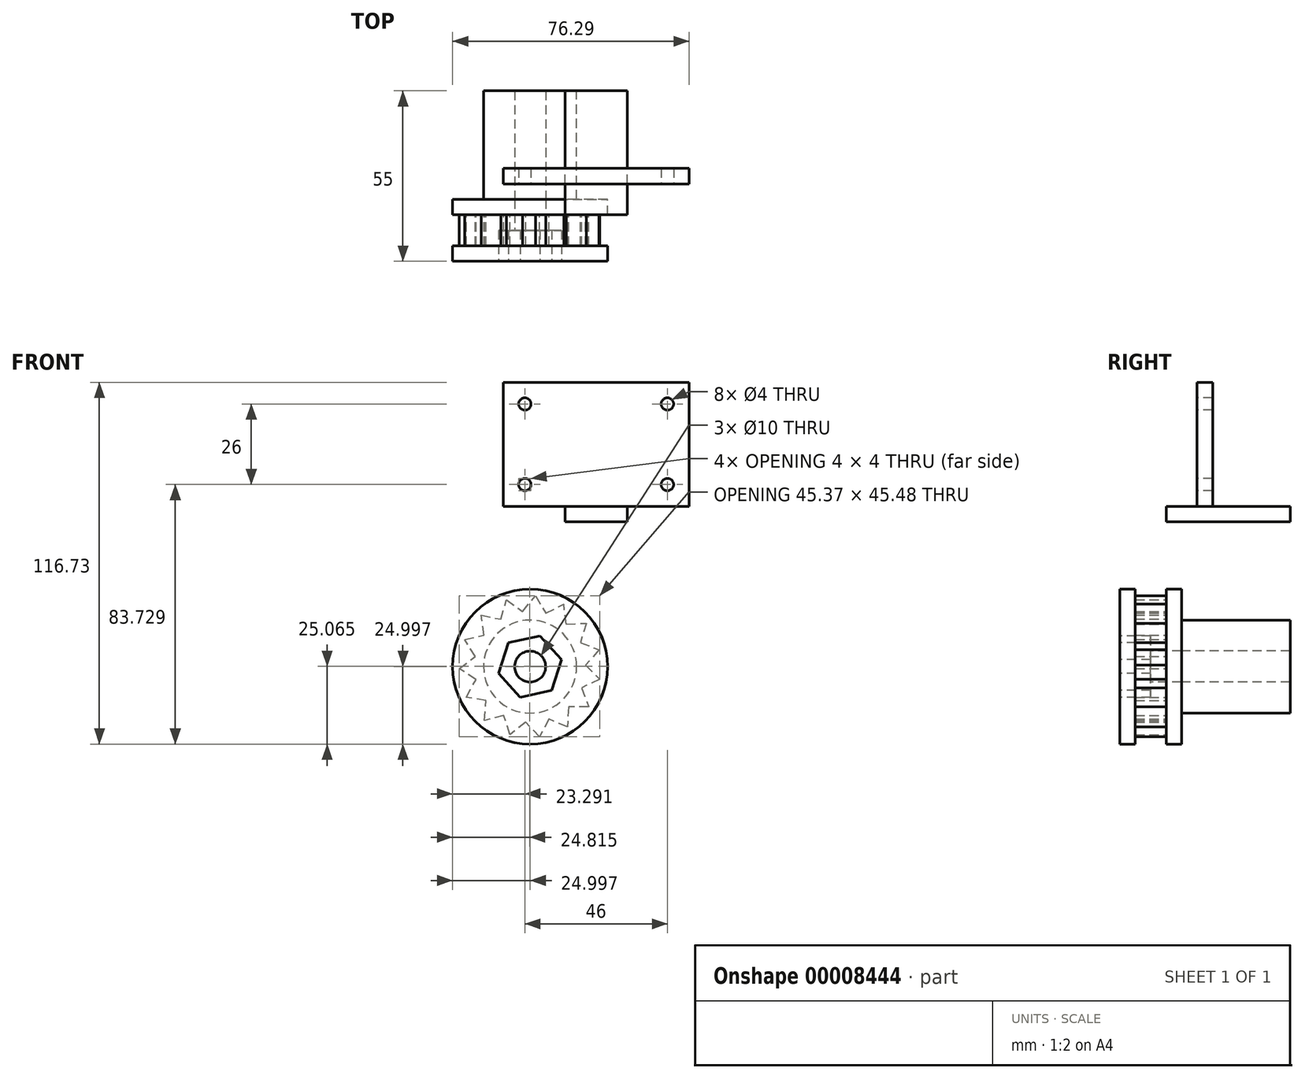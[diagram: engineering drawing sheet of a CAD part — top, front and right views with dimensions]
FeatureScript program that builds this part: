
annotation { "Feature Type Name" : "Feature", "Feature Type Description" : "" }
export const myFeature = defineFeature(function(context is Context, id is Id, definition is map)
    precondition{}
    {
        {
            var Q0;
            Q0=qCreatedBy(makeId("Front.planeOp"),FACE);
            var sketch = newSketch(context, id + "F0", { "sketchPlane" : qUnion([Q0])});
            skLineSegment(sketch, "E0", {"start": v(-23.94, 12.62) * mm, "end": v(-23.94, 7.62) * mm});
            skLineSegment(sketch, "E1", {"start": v(-23.94, 7.62) * mm, "end": v(-3.94, 7.62) * mm});
            skLineSegment(sketch, "E2", {"start": v(-3.94, 7.62) * mm, "end": v(-3.94, 12.62) * mm});
            skLineSegment(sketch, "E3", {"start": v(-3.94, 12.62) * mm, "end": v(16.06, 12.62) * mm});
            skLineSegment(sketch, "E4", {"start": v(16.06, 12.62) * mm, "end": v(16.06, 52.62) * mm});
            skLineSegment(sketch, "E5", {"start": v(16.06, 52.62) * mm, "end": v(-43.94, 52.62) * mm});
            skLineSegment(sketch, "E6", {"start": v(-43.94, 52.62) * mm, "end": v(-43.94, 12.62) * mm});
            skLineSegment(sketch, "E7", {"start": v(-43.94, 12.62) * mm, "end": v(-23.94, 12.62) * mm});
            skSolve(sketch);
        }
        {
            var Q0;
            Q0=makeQuery(id+"F0.imprint","IMPRINT",FACE,{"disambiguationData":[TD([[makeQuery(id+"F0.imprint","IMPRINT",EDGE,{"derivedFrom":sQuery(id+"F0.wireOp",EDGE,"E0")}),1.0]])]});
            extrude(context, id + "F1", {"entities" : qUnion([Q0]), "depth" : 40 * mm});
        }
        {
            var Q0;
            Q0=makeQuery(id+"F1.opExtrude","SWEPT_FACE",FACE,{"disambiguationData":[OSD([sQuery(id+"F0.wireOp",EDGE,"E6")])]});
            var sketch = newSketch(context, id + "F2", { "sketchPlane" : qUnion([Q0])});
            skLineSegment(sketch, "E8", {"start": v(40, 12.62) * mm, "end": v(30, 12.62) * mm});
            skLineSegment(sketch, "E9", {"start": v(30, 12.62) * mm, "end": v(30, 52.62) * mm});
            skLineSegment(sketch, "E10", {"start": v(30, 52.62) * mm, "end": v(40, 52.62) * mm});
            skLineSegment(sketch, "E11", {"start": v(40, 52.62) * mm, "end": v(40, 12.62) * mm});
            skSolve(sketch);
        }
        {
            var Q0;
            Q0=makeQuery(id+"F2.imprint","IMPRINT",FACE,{"disambiguationData":[TD([[makeQuery(id+"F2.imprint","IMPRINT",EDGE,{"derivedFrom":sQuery(id+"F2.wireOp",EDGE,"E8")}),-1.0]])]});
            var Q1;
            Q1=makeQuery(id+"F1.opExtrude","SWEPT_FACE",FACE,{"disambiguationData":[OSD([sQuery(id+"F0.wireOp",EDGE,"E4")])]});
            extrude(context, id + "F3", {"entities" : qUnion([Q0]), "operationType" : NewBodyOperationType.REMOVE, "endBound" : BoundingType.UP_TO_BODY, "oppositeDirection" : true, "endBoundEntityBody" : qUnion([Q1]), "depth" : 25 * mm});
        }
        {
            var Q0;
            Q0=makeQuery(id+"F1.opExtrude","SWEPT_FACE",FACE,{"disambiguationData":[OSD([sQuery(id+"F0.wireOp",EDGE,"E6")])]});
            var sketch = newSketch(context, id + "F4", { "sketchPlane" : qUnion([Q0])});
            skLineSegment(sketch, "E12.bottom", {"start": v(0, 52.62) * mm, "end": v(25, 52.62) * mm});
            skLineSegment(sketch, "E12.top", {"start": v(0, 12.62) * mm, "end": v(25, 12.62) * mm});
            skLineSegment(sketch, "E12.left", {"start": v(0, 52.62) * mm, "end": v(0, 12.62) * mm});
            skLineSegment(sketch, "E12.right", {"start": v(25, 52.62) * mm, "end": v(25, 12.62) * mm});
            skPoint(sketch, "E13", {"position": v(30, 52.62) * mm});
            skSolve(sketch);
        }
        {
            var Q0;
            Q0=makeQuery(id+"F4.imprint","IMPRINT",FACE,{"disambiguationData":[TD([[makeQuery(id+"F4.imprint","IMPRINT",EDGE,{"derivedFrom":sQuery(id+"F4.wireOp",EDGE,"E12.bottom")}),1.0]])]});
            extrude(context, id + "F5", {"entities" : qUnion([Q0]), "operationType" : NewBodyOperationType.REMOVE, "endBound" : BoundingType.THROUGH_ALL, "oppositeDirection" : true, "depth" : 25 * mm});
        }
        {
            var Q0;
            Q0=makeQuery(id+"F3.boolean.opBoolean","COPY",FACE,{"derivedFrom":makeQuery(id+"F3.opExtrude","SWEPT_FACE",FACE,{"disambiguationData":[OSD([sQuery(id+"F2.wireOp",EDGE,"E9")])]})});
            var sketch = newSketch(context, id + "F6", { "sketchPlane" : qUnion([Q0])});
            skCircle(sketch, "E14", {"center": v(-36.94, 45.62) * mm, "radius": 2 * mm});
            skCircle(sketch, "E15", {"center": v(-36.94, 19.62) * mm, "radius": 2 * mm});
            skCircle(sketch, "E16", {"center": v(9.06, 19.62) * mm, "radius": 2 * mm});
            skCircle(sketch, "E17", {"center": v(9.06, 45.62) * mm, "radius": 2 * mm});
            skSolve(sketch);
        }
        {
            var Q0;
            Q0=makeQuery(id+"F6.imprint","IMPRINT",FACE,{"disambiguationData":[TD([[makeQuery(id+"F6.imprint","IMPRINT",EDGE,{"derivedFrom":sQuery(id+"F6.wireOp",EDGE,"E14")}),1.0]])]});
            var Q1;
            Q1=makeQuery(id+"F6.imprint","IMPRINT",FACE,{"disambiguationData":[TD([[makeQuery(id+"F6.imprint","IMPRINT",EDGE,{"derivedFrom":sQuery(id+"F6.wireOp",EDGE,"E17")}),1.0]])]});
            var Q2;
            Q2=makeQuery(id+"F6.imprint","IMPRINT",FACE,{"disambiguationData":[TD([[makeQuery(id+"F6.imprint","IMPRINT",EDGE,{"derivedFrom":sQuery(id+"F6.wireOp",EDGE,"E16")}),1.0]])]});
            var Q3;
            Q3=makeQuery(id+"F6.imprint","IMPRINT",FACE,{"disambiguationData":[TD([[makeQuery(id+"F6.imprint","IMPRINT",EDGE,{"derivedFrom":sQuery(id+"F6.wireOp",EDGE,"E15")}),1.0]])]});
            extrude(context, id + "F7", {"entities" : qUnion([Q0, Q1, Q2, Q3]), "operationType" : NewBodyOperationType.REMOVE, "endBound" : BoundingType.THROUGH_ALL, "oppositeDirection" : true, "depth" : 25 * mm});
        }
        {
            var Q0;
            Q0=qCreatedBy(makeId("Front.planeOp"),FACE);
            var sketch = newSketch(context, id + "F8", { "sketchPlane" : qUnion([Q0])});
            skCircle(sketch, "E18", {"center": v(-35.23, -39.11) * mm, "radius": 15 * mm});
            skSolve(sketch);
        }
        {
            var Q0;
            Q0=makeQuery(id+"F8.imprint","IMPRINT",FACE,{"disambiguationData":[TD([[makeQuery(id+"F8.imprint","IMPRINT",EDGE,{"derivedFrom":sQuery(id+"F8.wireOp",EDGE,"E18")}),1.0]])]});
            extrude(context, id + "F9", {"entities" : qUnion([Q0]), "depth" : 35 * mm});
        }
        {
            var Q0;
            Q0=makeQuery(id+"F9.opExtrude","CAP_FACE",FACE,{"disambiguationData":[OSD([sQuery(id+"F8.wireOp",EDGE,"E18")])],"isStart":false});
            var sketch = newSketch(context, id + "F10", { "sketchPlane" : qUnion([Q0])});
            skPoint(sketch, "E19", {"position": v(-35.23, -39.11) * mm});
            skCircle(sketch, "E20", {"center": v(-35.23, -39.11) * mm, "radius": 25 * mm});
            skSolve(sketch);
        }
        {
            var Q0;
            Q0=makeQuery(id+"F10.imprint","IMPRINT",FACE,{"disambiguationData":[TD([[makeQuery(id+"F10.imprint","IMPRINT",EDGE,{"derivedFrom":sQuery(id+"F10.wireOp",EDGE,"E20")}),1.0]])]});
            var Q1;
            Q1=makeQuery(id+"F10.imprint","IMPRINT",FACE,{"disambiguationData":[TD([[makeQuery(id+"F10.imprint","IMPRINT",EDGE,{"derivedFrom":makeQuery(id+"F9.opExtrude","CAP_EDGE",EDGE,{"disambiguationData":[OSD([sQuery(id+"F8.wireOp",EDGE,"E18")])],"isStart":false})}),1.0]])]});
            extrude(context, id + "F11", {"entities" : qUnion([Q0, Q1]), "depth" : 5 * mm});
        }
        {
            var Q0;
            Q0=makeQuery(id+"F11.opExtrude","CAP_FACE",FACE,{"disambiguationData":[OSD([sQuery(id+"F10.wireOp",EDGE,"E20")])],"isStart":false});
            var sketch = newSketch(context, id + "F12", { "sketchPlane" : qUnion([Q0])});
            skPoint(sketch, "E21", {"position": v(-35.23, -39.11) * mm});
            skCircle(sketch, "E22.cCircle", {"center": v(-35.23, -39.11) * mm, "radius": 17.56 * mm, "construction": true});
            skLineSegment(sketch, "E22.0", {"start": v(-23.6, -25.44) * mm, "end": v(-19.05, -31.35) * mm});
            skLineSegment(sketch, "E22.1", {"start": v(-19.05, -31.35) * mm, "end": v(-17.29, -38.6) * mm});
            skLineSegment(sketch, "E22.2", {"start": v(-17.29, -38.6) * mm, "end": v(-18.63, -45.94) * mm});
            skLineSegment(sketch, "E22.3", {"start": v(-18.63, -45.94) * mm, "end": v(-22.85, -52.1) * mm});
            skLineSegment(sketch, "E22.4", {"start": v(-22.85, -52.1) * mm, "end": v(-29.2, -56.02) * mm});
            skLineSegment(sketch, "E22.5", {"start": v(-29.2, -56.02) * mm, "end": v(-36.6, -57.01) * mm});
            skLineSegment(sketch, "E22.6", {"start": v(-36.6, -57.01) * mm, "end": v(-43.76, -54.9) * mm});
            skLineSegment(sketch, "E22.7", {"start": v(-43.76, -54.9) * mm, "end": v(-49.45, -50.07) * mm});
            skLineSegment(sketch, "E22.8", {"start": v(-49.45, -50.07) * mm, "end": v(-52.68, -43.34) * mm});
            skLineSegment(sketch, "E22.9", {"start": v(-52.68, -43.34) * mm, "end": v(-52.9, -35.88) * mm});
            skLineSegment(sketch, "E22.10", {"start": v(-52.9, -35.88) * mm, "end": v(-50.05, -28.98) * mm});
            skLineSegment(sketch, "E22.11", {"start": v(-50.05, -28.98) * mm, "end": v(-44.65, -23.83) * mm});
            skLineSegment(sketch, "E22.12", {"start": v(-44.65, -23.83) * mm, "end": v(-37.62, -21.32) * mm});
            skLineSegment(sketch, "E22.13", {"start": v(-37.62, -21.32) * mm, "end": v(-30.17, -21.89) * mm});
            skLineSegment(sketch, "E22.14", {"start": v(-30.17, -21.89) * mm, "end": v(-23.6, -25.44) * mm});
            skPoint(sketch, "E22.0.midPoint", {"position": v(-21.33, -28.4) * mm});
            skCircle(sketch, "E23.cCircle", {"center": v(-35.23, -39.11) * mm, "radius": 22.38 * mm, "construction": true});
            skLineSegment(sketch, "E23.0", {"start": v(-24.36, -18.99) * mm, "end": v(-17.12, -25.15) * mm});
            skLineSegment(sketch, "E23.1", {"start": v(-17.12, -25.15) * mm, "end": v(-13, -33.72) * mm});
            skLineSegment(sketch, "E23.2", {"start": v(-13, -33.72) * mm, "end": v(-12.73, -43.23) * mm});
            skLineSegment(sketch, "E23.3", {"start": v(-12.73, -43.23) * mm, "end": v(-16.35, -52.03) * mm});
            skLineSegment(sketch, "E23.4", {"start": v(-16.35, -52.03) * mm, "end": v(-23.24, -58.59) * mm});
            skLineSegment(sketch, "E23.5", {"start": v(-23.24, -58.59) * mm, "end": v(-32.2, -61.79) * mm});
            skLineSegment(sketch, "E23.6", {"start": v(-32.2, -61.79) * mm, "end": v(-41.68, -61.06) * mm});
            skLineSegment(sketch, "E23.7", {"start": v(-41.68, -61.06) * mm, "end": v(-50.05, -56.54) * mm});
            skLineSegment(sketch, "E23.8", {"start": v(-50.05, -56.54) * mm, "end": v(-55.86, -49) * mm});
            skLineSegment(sketch, "E23.9", {"start": v(-55.86, -49) * mm, "end": v(-58.1, -39.76) * mm});
            skLineSegment(sketch, "E23.10", {"start": v(-58.1, -39.76) * mm, "end": v(-56.39, -30.4) * mm});
            skLineSegment(sketch, "E23.11", {"start": v(-56.39, -30.4) * mm, "end": v(-51.02, -22.56) * mm});
            skLineSegment(sketch, "E23.12", {"start": v(-51.02, -22.56) * mm, "end": v(-42.92, -17.57) * mm});
            skLineSegment(sketch, "E23.13", {"start": v(-42.92, -17.57) * mm, "end": v(-33.49, -16.3) * mm});
            skLineSegment(sketch, "E23.14", {"start": v(-33.49, -16.3) * mm, "end": v(-24.36, -18.99) * mm});
            skPoint(sketch, "E23.0.midPoint", {"position": v(-20.74, -22.07) * mm});
            skPoint(sketch, "E24", {"position": v(-26.89, -23.66) * mm});
            skLineSegment(sketch, "E25", {"start": v(-35.23, -39.11) * mm, "end": v(-24.36, -18.99) * mm, "construction": true});
            skLineSegment(sketch, "E26", {"start": v(-30.17, -21.89) * mm, "end": v(-24.36, -18.99) * mm});
            skLineSegment(sketch, "E27", {"start": v(-23.6, -25.44) * mm, "end": v(-24.36, -18.99) * mm});
            skLineSegment(sketch, "E28", {"start": v(-23.6, -25.44) * mm, "end": v(-17.12, -25.15) * mm});
            skLineSegment(sketch, "E29", {"start": v(-17.12, -25.15) * mm, "end": v(-19.05, -31.35) * mm});
            skLineSegment(sketch, "E30", {"start": v(-19.05, -31.35) * mm, "end": v(-13, -33.72) * mm});
            skLineSegment(sketch, "E31", {"start": v(-13, -33.72) * mm, "end": v(-17.29, -38.6) * mm});
            skLineSegment(sketch, "E32", {"start": v(-17.29, -38.6) * mm, "end": v(-12.73, -43.23) * mm});
            skLineSegment(sketch, "E33", {"start": v(-12.73, -43.23) * mm, "end": v(-18.63, -45.94) * mm});
            skLineSegment(sketch, "E34", {"start": v(-18.63, -45.94) * mm, "end": v(-16.35, -52.03) * mm});
            skLineSegment(sketch, "E35", {"start": v(-16.35, -52.03) * mm, "end": v(-22.85, -52.1) * mm});
            skLineSegment(sketch, "E36", {"start": v(-22.85, -52.1) * mm, "end": v(-23.24, -58.59) * mm});
            skLineSegment(sketch, "E37", {"start": v(-23.24, -58.59) * mm, "end": v(-29.2, -56.02) * mm});
            skLineSegment(sketch, "E38", {"start": v(-29.2, -56.02) * mm, "end": v(-32.2, -61.79) * mm});
            skLineSegment(sketch, "E39", {"start": v(-32.2, -61.79) * mm, "end": v(-36.6, -57.01) * mm});
            skLineSegment(sketch, "E40", {"start": v(-36.6, -57.01) * mm, "end": v(-41.68, -61.06) * mm});
            skLineSegment(sketch, "E41", {"start": v(-41.68, -61.06) * mm, "end": v(-43.76, -54.9) * mm});
            skLineSegment(sketch, "E42", {"start": v(-43.76, -54.9) * mm, "end": v(-50.05, -56.54) * mm});
            skLineSegment(sketch, "E43", {"start": v(-50.05, -56.54) * mm, "end": v(-49.45, -50.07) * mm});
            skLineSegment(sketch, "E44", {"start": v(-49.45, -50.07) * mm, "end": v(-55.86, -49) * mm});
            skLineSegment(sketch, "E45", {"start": v(-55.86, -49) * mm, "end": v(-52.68, -43.34) * mm});
            skLineSegment(sketch, "E46", {"start": v(-52.68, -43.34) * mm, "end": v(-58.1, -39.76) * mm});
            skLineSegment(sketch, "E47", {"start": v(-58.1, -39.76) * mm, "end": v(-52.9, -35.88) * mm});
            skLineSegment(sketch, "E48", {"start": v(-52.9, -35.88) * mm, "end": v(-56.39, -30.4) * mm});
            skLineSegment(sketch, "E49", {"start": v(-56.39, -30.4) * mm, "end": v(-50.05, -28.98) * mm});
            skLineSegment(sketch, "E50", {"start": v(-50.05, -28.98) * mm, "end": v(-51.02, -22.56) * mm});
            skLineSegment(sketch, "E51", {"start": v(-51.02, -22.56) * mm, "end": v(-44.65, -23.83) * mm});
            skLineSegment(sketch, "E52", {"start": v(-44.65, -23.83) * mm, "end": v(-42.92, -17.57) * mm});
            skLineSegment(sketch, "E53", {"start": v(-42.92, -17.57) * mm, "end": v(-37.62, -21.32) * mm});
            skLineSegment(sketch, "E54", {"start": v(-37.62, -21.32) * mm, "end": v(-33.49, -16.3) * mm});
            skLineSegment(sketch, "E55", {"start": v(-33.49, -16.3) * mm, "end": v(-30.17, -21.89) * mm});
            skSolve(sketch);
        }
        {
            var Q0;
            Q0=makeQuery(id+"F12.imprint","IMPRINT",FACE,{"disambiguationData":[TD([[makeQuery(id+"F12.imprint","IMPRINT",EDGE,{"derivedFrom":sQuery(id+"F12.wireOp",EDGE,"E22.0")}),-1.0]])]});
            var Q1;
            Q1=makeQuery(id+"F12.imprint","IMPRINT",FACE,{"disambiguationData":[TD([[makeQuery(id+"F12.imprint","IMPRINT",EDGE,{"derivedFrom":sQuery(id+"F12.wireOp",EDGE,"E22.13")}),1.0]])]});
            var Q2;
            Q2=makeQuery(id+"F12.imprint","IMPRINT",FACE,{"disambiguationData":[TD([[makeQuery(id+"F12.imprint","IMPRINT",EDGE,{"derivedFrom":sQuery(id+"F12.wireOp",EDGE,"E22.14")}),1.0]])]});
            var Q3;
            Q3=makeQuery(id+"F12.imprint","IMPRINT",FACE,{"disambiguationData":[TD([[makeQuery(id+"F12.imprint","IMPRINT",EDGE,{"derivedFrom":sQuery(id+"F12.wireOp",EDGE,"E22.0")}),1.0]])]});
            var Q4;
            Q4=makeQuery(id+"F12.imprint","IMPRINT",FACE,{"disambiguationData":[TD([[makeQuery(id+"F12.imprint","IMPRINT",EDGE,{"derivedFrom":sQuery(id+"F12.wireOp",EDGE,"E22.1")}),1.0]])]});
            var Q5;
            Q5=makeQuery(id+"F12.imprint","IMPRINT",FACE,{"disambiguationData":[TD([[makeQuery(id+"F12.imprint","IMPRINT",EDGE,{"derivedFrom":sQuery(id+"F12.wireOp",EDGE,"E22.2")}),1.0]])]});
            var Q6;
            Q6=makeQuery(id+"F12.imprint","IMPRINT",FACE,{"disambiguationData":[TD([[makeQuery(id+"F12.imprint","IMPRINT",EDGE,{"derivedFrom":sQuery(id+"F12.wireOp",EDGE,"E22.3")}),1.0]])]});
            var Q7;
            Q7=makeQuery(id+"F12.imprint","IMPRINT",FACE,{"disambiguationData":[TD([[makeQuery(id+"F12.imprint","IMPRINT",EDGE,{"derivedFrom":sQuery(id+"F12.wireOp",EDGE,"E22.4")}),1.0]])]});
            var Q8;
            Q8=makeQuery(id+"F12.imprint","IMPRINT",FACE,{"disambiguationData":[TD([[makeQuery(id+"F12.imprint","IMPRINT",EDGE,{"derivedFrom":sQuery(id+"F12.wireOp",EDGE,"E22.5")}),1.0]])]});
            var Q9;
            Q9=makeQuery(id+"F12.imprint","IMPRINT",FACE,{"disambiguationData":[TD([[makeQuery(id+"F12.imprint","IMPRINT",EDGE,{"derivedFrom":sQuery(id+"F12.wireOp",EDGE,"E22.6")}),1.0]])]});
            var Q10;
            Q10=makeQuery(id+"F12.imprint","IMPRINT",FACE,{"disambiguationData":[TD([[makeQuery(id+"F12.imprint","IMPRINT",EDGE,{"derivedFrom":sQuery(id+"F12.wireOp",EDGE,"E22.7")}),1.0]])]});
            var Q11;
            Q11=makeQuery(id+"F12.imprint","IMPRINT",FACE,{"disambiguationData":[TD([[makeQuery(id+"F12.imprint","IMPRINT",EDGE,{"derivedFrom":sQuery(id+"F12.wireOp",EDGE,"E22.8")}),1.0]])]});
            var Q12;
            Q12=makeQuery(id+"F12.imprint","IMPRINT",FACE,{"disambiguationData":[TD([[makeQuery(id+"F12.imprint","IMPRINT",EDGE,{"derivedFrom":sQuery(id+"F12.wireOp",EDGE,"E22.9")}),1.0]])]});
            var Q13;
            Q13=makeQuery(id+"F12.imprint","IMPRINT",FACE,{"disambiguationData":[TD([[makeQuery(id+"F12.imprint","IMPRINT",EDGE,{"derivedFrom":sQuery(id+"F12.wireOp",EDGE,"E22.10")}),1.0]])]});
            var Q14;
            Q14=makeQuery(id+"F12.imprint","IMPRINT",FACE,{"disambiguationData":[TD([[makeQuery(id+"F12.imprint","IMPRINT",EDGE,{"derivedFrom":sQuery(id+"F12.wireOp",EDGE,"E22.11")}),1.0]])]});
            var Q15;
            Q15=makeQuery(id+"F12.imprint","IMPRINT",FACE,{"disambiguationData":[TD([[makeQuery(id+"F12.imprint","IMPRINT",EDGE,{"derivedFrom":sQuery(id+"F12.wireOp",EDGE,"E22.12")}),1.0]])]});
            extrude(context, id + "F13", {"entities" : qUnion([Q0, Q1, Q2, Q3, Q4, Q5, Q6, Q7, Q8, Q9, Q10, Q11, Q12, Q13, Q14, Q15]), "operationType" : NewBodyOperationType.ADD, "depth" : 10 * mm});
        }
        {
            var Q0;
            Q0=makeQuery(id+"F13.opExtrude","CAP_FACE",FACE,{"disambiguationData":[OSD([sQuery(id+"F12.wireOp",EDGE,"E26"),sQuery(id+"F12.wireOp",EDGE,"E27"),sQuery(id+"F12.wireOp",EDGE,"E28"),sQuery(id+"F12.wireOp",EDGE,"E29"),sQuery(id+"F12.wireOp",EDGE,"E30"),sQuery(id+"F12.wireOp",EDGE,"E31"),sQuery(id+"F12.wireOp",EDGE,"E32"),sQuery(id+"F12.wireOp",EDGE,"E33"),sQuery(id+"F12.wireOp",EDGE,"E34"),sQuery(id+"F12.wireOp",EDGE,"E35"),sQuery(id+"F12.wireOp",EDGE,"E36"),sQuery(id+"F12.wireOp",EDGE,"E37"),sQuery(id+"F12.wireOp",EDGE,"E38"),sQuery(id+"F12.wireOp",EDGE,"E39"),sQuery(id+"F12.wireOp",EDGE,"E40"),sQuery(id+"F12.wireOp",EDGE,"E41"),sQuery(id+"F12.wireOp",EDGE,"E42"),sQuery(id+"F12.wireOp",EDGE,"E43"),sQuery(id+"F12.wireOp",EDGE,"E44"),sQuery(id+"F12.wireOp",EDGE,"E45"),sQuery(id+"F12.wireOp",EDGE,"E46"),sQuery(id+"F12.wireOp",EDGE,"E47"),sQuery(id+"F12.wireOp",EDGE,"E48"),sQuery(id+"F12.wireOp",EDGE,"E49"),sQuery(id+"F12.wireOp",EDGE,"E50"),sQuery(id+"F12.wireOp",EDGE,"E51"),sQuery(id+"F12.wireOp",EDGE,"E52"),sQuery(id+"F12.wireOp",EDGE,"E53"),sQuery(id+"F12.wireOp",EDGE,"E54"),sQuery(id+"F12.wireOp",EDGE,"E55")])],"isStart":false});
            var sketch = newSketch(context, id + "F14", { "sketchPlane" : qUnion([Q0])});
            skLineSegment(sketch, "E56", {"start": v(-30.17, -21.89) * mm, "end": v(-29.2, -56.02) * mm, "construction": true});
            skLineSegment(sketch, "E57", {"start": v(-50.05, -28.98) * mm, "end": v(-17.29, -38.6) * mm, "construction": true});
            skLineSegment(sketch, "E58", {"start": v(-17.29, -38.6) * mm, "end": v(-49.45, -50.07) * mm, "construction": true});
            skLineSegment(sketch, "E59", {"start": v(-49.45, -50.07) * mm, "end": v(-30.17, -21.89) * mm, "construction": true});
            skLineSegment(sketch, "E60", {"start": v(-50.05, -28.98) * mm, "end": v(-29.2, -56.02) * mm, "construction": true});
            skPoint(sketch, "E61", {"position": v(-37.54, -32.65) * mm});
            skPoint(sketch, "E62", {"position": v(-29.57, -42.98) * mm});
            skPoint(sketch, "E63", {"position": v(-37.17, -45.7) * mm});
            skPoint(sketch, "E64", {"position": v(-42.09, -39.3) * mm});
            skPoint(sketch, "E65", {"position": v(-29.8, -34.93) * mm});
            skPoint(sketch, "E66", {"position": v(-39.63, -42.5) * mm});
            skPoint(sketch, "E67", {"position": v(-33.37, -44.34) * mm});
            skPoint(sketch, "E68", {"position": v(-39.81, -35.98) * mm});
            skPoint(sketch, "E69", {"position": v(-33.67, -33.8) * mm});
            skPoint(sketch, "E70", {"position": v(-29.69, -38.96) * mm});
            skLineSegment(sketch, "E71", {"start": v(-42.09, -39.3) * mm, "end": v(-29.69, -38.96) * mm, "construction": true});
            skLineSegment(sketch, "E72", {"start": v(-29.8, -34.93) * mm, "end": v(-39.63, -42.5) * mm, "construction": true});
            skLineSegment(sketch, "E73", {"start": v(-33.37, -44.34) * mm, "end": v(-37.54, -32.65) * mm, "construction": true});
            skLineSegment(sketch, "E74", {"start": v(-39.81, -35.98) * mm, "end": v(-29.57, -42.98) * mm, "construction": true});
            skPoint(sketch, "E75", {"position": v(-35.23, -39.11) * mm});
            skCircle(sketch, "E76", {"center": v(-35.23, -39.11) * mm, "radius": 24.99 * mm});
            skSolve(sketch);
        }
        {
            var Q0;
            Q0 = qSketchRegion(id + "F14", true);
            extrude(context, id + "F15", {"entities" : qUnion([Q0]), "operationType" : NewBodyOperationType.ADD, "depth" : 5 * mm});
        }
        {
            var Q0;
            Q0=makeQuery(id+"F15.opExtrude","CAP_FACE",FACE,{"disambiguationData":[OSD([sQuery(id+"F14.wireOp",EDGE,"E76")])],"isStart":false});
            var sketch = newSketch(context, id + "F16", { "sketchPlane" : qUnion([Q0])});
            skPoint(sketch, "E77", {"position": v(-35.23, -39.11) * mm});
            skCircle(sketch, "E78", {"center": v(-35.23, -39.11) * mm, "radius": 5 * mm});
            skSolve(sketch);
        }
        {
            var Q0;
            Q0=makeQuery(id+"F15.opExtrude","CAP_FACE",FACE,{"disambiguationData":[OSD([sQuery(id+"F14.wireOp",EDGE,"E76")])],"isStart":false});
            var sketch = newSketch(context, id + "F17", { "sketchPlane" : qUnion([Q0])});
            skPoint(sketch, "E79", {"position": v(-35.23, -39.11) * mm});
            skCircle(sketch, "E80.cCircle", {"center": v(-35.23, -39.11) * mm, "radius": 9 * mm, "construction": true});
            skLineSegment(sketch, "E80.0", {"start": v(-32.07, -29.21) * mm, "end": v(-25.08, -36.9) * mm});
            skLineSegment(sketch, "E80.1", {"start": v(-25.08, -36.9) * mm, "end": v(-28.24, -46.8) * mm});
            skLineSegment(sketch, "E80.2", {"start": v(-28.24, -46.8) * mm, "end": v(-38.4, -49.01) * mm});
            skLineSegment(sketch, "E80.3", {"start": v(-38.4, -49.01) * mm, "end": v(-45.39, -41.32) * mm});
            skLineSegment(sketch, "E80.4", {"start": v(-45.39, -41.32) * mm, "end": v(-42.22, -31.42) * mm});
            skLineSegment(sketch, "E80.5", {"start": v(-42.22, -31.42) * mm, "end": v(-32.07, -29.21) * mm});
            skPoint(sketch, "E80.0.midPoint", {"position": v(-28.57, -33.06) * mm});
            skSolve(sketch);
        }
        {
            var Q0;
            Q0=makeQuery(id+"F16.imprint","IMPRINT",FACE,{"disambiguationData":[TD([[makeQuery(id+"F16.imprint","IMPRINT",EDGE,{"derivedFrom":sQuery(id+"F16.wireOp",EDGE,"E78")}),1.0]])]});
            var Q1;
            Q1=sQuery(id+"F16.wireOp",EDGE,"E78");
            extrude(context, id + "F18", {"entities" : qUnion([Q0]), "operationType" : NewBodyOperationType.REMOVE, "surfaceEntities" : qUnion([Q1]), "endBound" : BoundingType.THROUGH_ALL, "oppositeDirection" : true, "depth" : 25 * mm});
        }
        {
            var Q0;
            Q0=makeQuery(id+"F17.imprint","IMPRINT",FACE,{"disambiguationData":[TD([[makeQuery(id+"F17.imprint","IMPRINT",EDGE,{"derivedFrom":sQuery(id+"F17.wireOp",EDGE,"E80.0")}),-1.0]])]});
            extrude(context, id + "F19", {"entities" : qUnion([Q0]), "operationType" : NewBodyOperationType.REMOVE, "oppositeDirection" : true, "depth" : 10 * mm});
        }
    });
